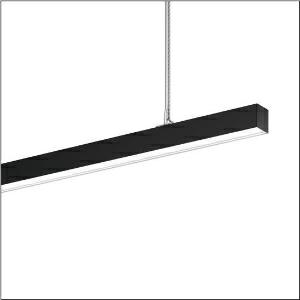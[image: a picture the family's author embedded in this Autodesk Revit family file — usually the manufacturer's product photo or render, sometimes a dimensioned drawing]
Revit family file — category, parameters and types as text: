
# Revit family: silica_21_51mx30tat4b
name_source: partatom
category: Lighting Fixtures
units: mm (PartAtom-declared; Revit-internal decimal feet)

## family parameters
Cut with Voids When Loaded = No
Host = Face
Light Source = No
Part Type = Normal
Room Calculation Point = No
Round Connector Dimension = Use Diameter
Shared = No

## types (1)
- --- (1 x LED, 4120 lm, 33.8 W, 6500K)
    Apparent Load = 34 VA
    CIE Flux Codes = 47 79 96 58 100
    Color Rendering = 80
    Color Temperature = 6500K
    Default Elevation = 1800 mm
    Description = Silica 21, office luminaire, primary optical cover: cover, of PMMA, opal, light emission: direct/indirect distribution, primary light characteristic: symmetric, installation type: suspended mounting, LED, rated luminous flux: 4.120lm, luminous efficacy: 116lm/W, light colour: 8tw, colour temperature: 2700..6500K, control gear: DALI DT8, with terminal, 3+2-pole, max. 2.5mm², mains connection: 220..240V, AC, 50/60Hz, rated input power: 35.5W, luminaire housing, of aluminium, matt jet black (RAL 9005), length: 1.204mm, width: 53mm, height: 53mm, protection rating (complete): IP20, insulation class (complete): insulation class I (protective earthing), certification: CE, permissible operating ambient temperature: 0..+35°C, standard: EN 50419, packaging unit: 1 piece
    Height = 53 mm
    Lamp = 1 x LED
    Lamp Light Flux = 4120 lm
    Lamp Power = 33.8 W
    Lamp count = 1
    Length = 1204 mm
    Luminous efficacy = 122 lm/W
    Manufacturer = Siteco
    ModVariant = No
    Model = 51MX30TAT4B
    Mounting Place = Ceiling
    Mounting Type = Pendant
    Number of Poles = 1
    OnlyDefault = Yes
    Power Factor = 1
    Product Name = Silica 21
    Product group = office luminaire | ceiling pendant
    ProductGroupID = 903
    Protection Class = Protection class I
    Protection Degree = IP 20
    RLX_Detail_Level = 1
    RLX_Emergency_Light_Flux = 0 lm
    RLX_Emergency_Type = 0
    RLX_Emergency_Type_DB = No
    RlxData = <blob elided: 22837 chars, md5=ed3b6503>
    Socket = socket
    Standby Power = 0 W
    System Light Flux = 4120 lm
    System Power = 34 W
    Type Comments = individual setting
    Type Image = l_1335856.jpg
    URL = http://relux.com
    VarID = @adj_140689
    Voltage = 0 V
    Weight = 0.00 kg
    Width = 53 mm

## geometry (parser evidence)
native form markers: Blend x4, Sweep x11
no freeform markers — native parametric forms only
